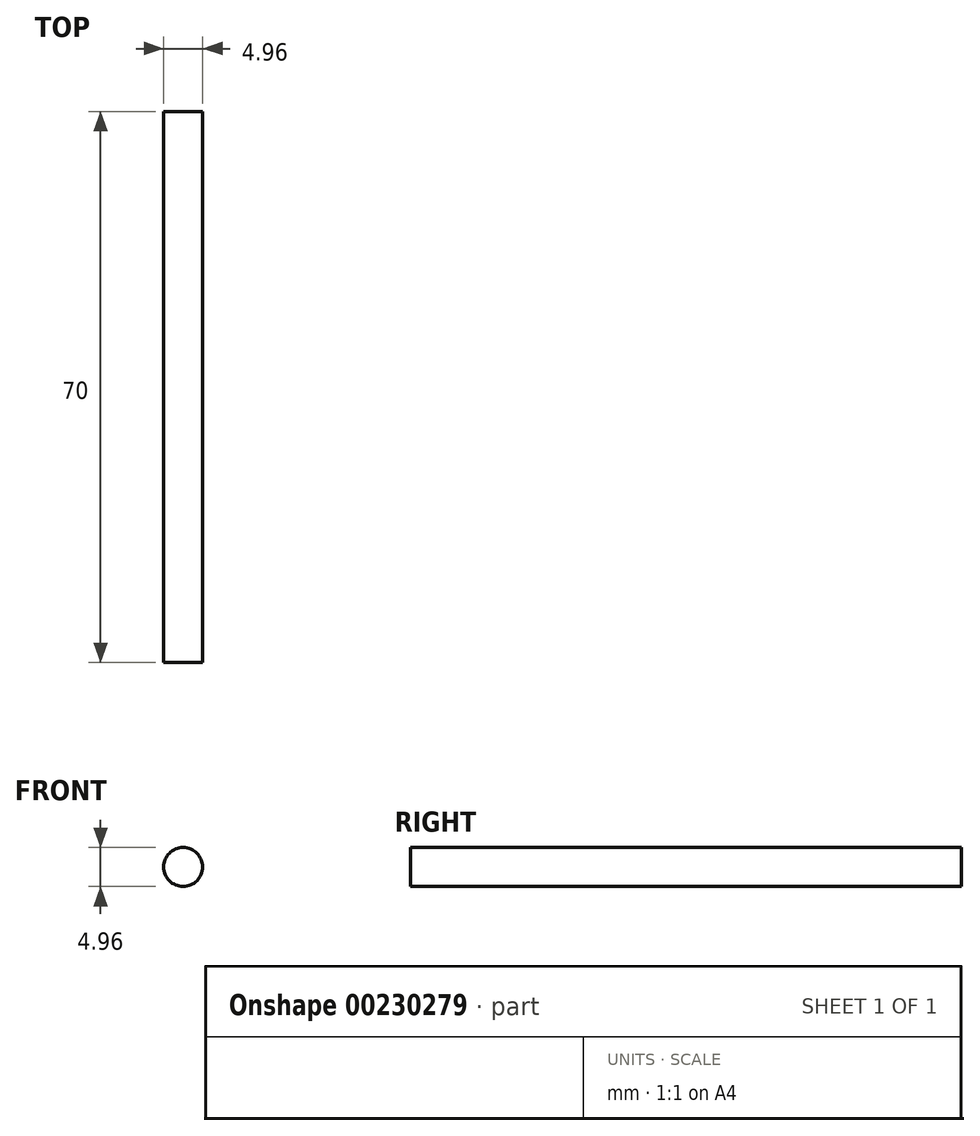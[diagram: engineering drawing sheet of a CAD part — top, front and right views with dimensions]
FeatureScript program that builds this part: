
annotation { "Feature Type Name" : "Feature", "Feature Type Description" : "" }
export const myFeature = defineFeature(function(context is Context, id is Id, definition is map)
    precondition{}
    {
        {
            var Q0;
            Q0=qCreatedBy(makeId("Front.planeOp"),FACE);
            var sketch = newSketch(context, id + "F0", { "sketchPlane" : qUnion([Q0])});
            skCircle(sketch, "E0", {"center": v(0, 0) * mm, "radius": 2.48 * mm});
            skSolve(sketch);
        }
        {
            var Q0;
            Q0=makeQuery(id+"F0.imprint","IMPRINT",FACE,{"disambiguationData":[TD([[makeQuery(id+"F0.imprint","IMPRINT",EDGE,{"derivedFrom":sQuery(id+"F0.wireOp",EDGE,"E0")}),1.0]])]});
            extrude(context, id + "F1", {"entities" : qUnion([Q0]), "depth" : 70 * mm});
        }
    });
